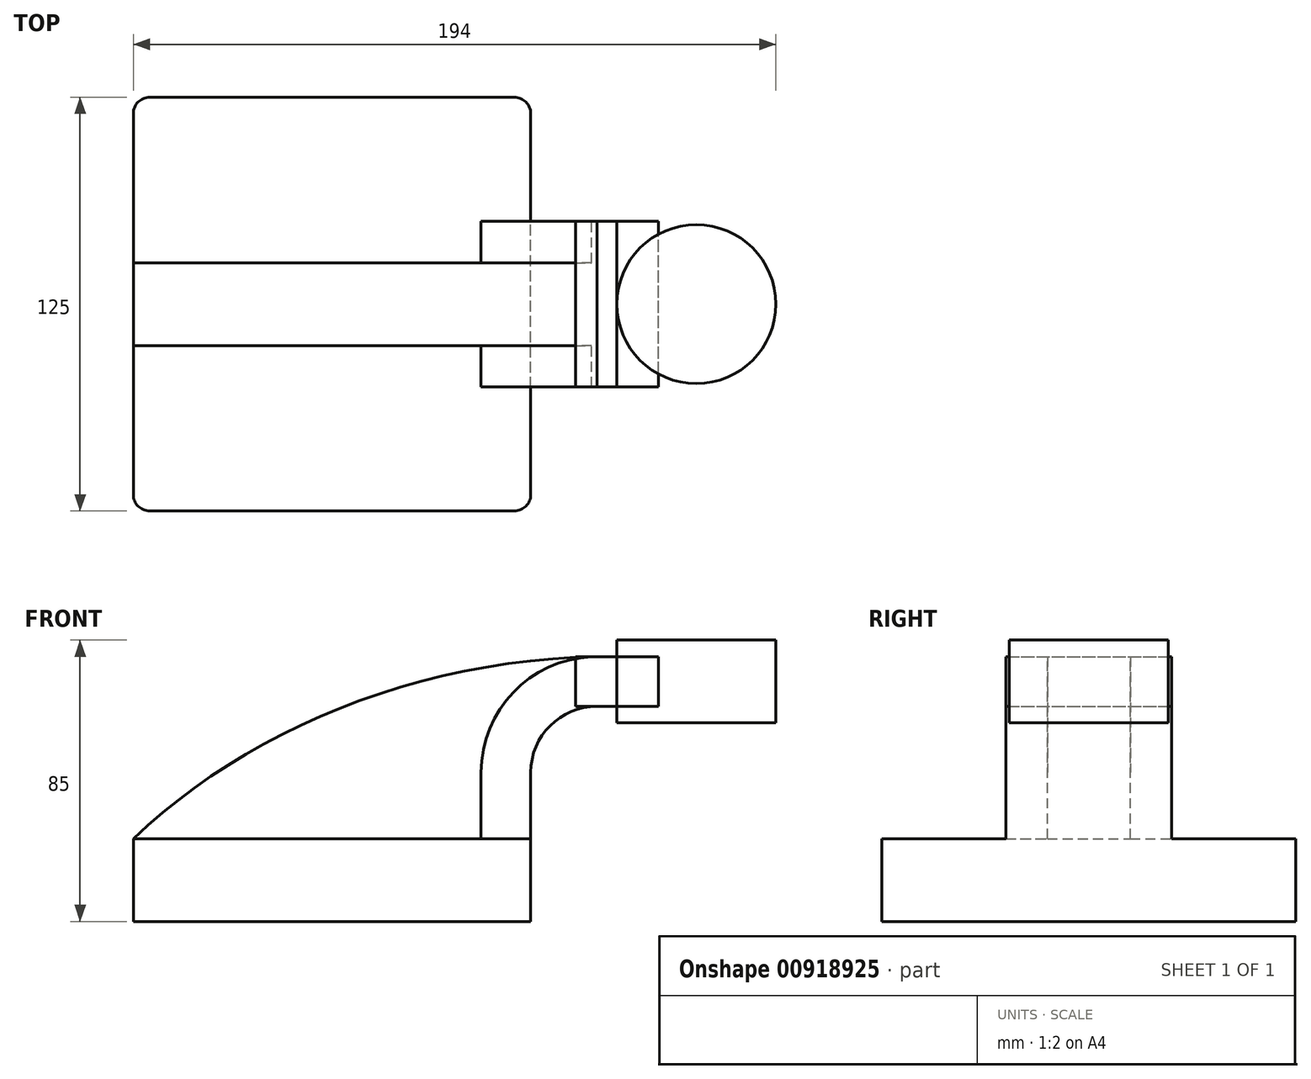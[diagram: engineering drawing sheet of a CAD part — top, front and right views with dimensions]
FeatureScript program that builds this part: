
annotation { "Feature Type Name" : "Feature", "Feature Type Description" : "" }
export const myFeature = defineFeature(function(context is Context, id is Id, definition is map)
    precondition{}
    {
        {
            var Q0;
            Q0=qCreatedBy(makeId("Front.planeOp"),FACE);
            var sketch = newSketch(context, id + "F0", { "sketchPlane" : qUnion([Q0])});
            skLineSegment(sketch, "E0.bottom", {"start": v(-60, 12.5) * mm, "end": v(60, 12.5) * mm});
            skLineSegment(sketch, "E0.top", {"start": v(-60, -12.5) * mm, "end": v(60, -12.5) * mm});
            skLineSegment(sketch, "E0.left", {"start": v(-60, 12.5) * mm, "end": v(-60, -12.5) * mm});
            skLineSegment(sketch, "E0.right", {"start": v(60, 12.5) * mm, "end": v(60, -12.5) * mm});
            skPoint(sketch, "E0.middle", {"position": v(0, 0) * mm});
            skLineSegment(sketch, "E1.bottom", {"start": v(134, 72.5) * mm, "end": v(86, 72.5) * mm});
            skLineSegment(sketch, "E1.top", {"start": v(134, 47.5) * mm, "end": v(86, 47.5) * mm});
            skLineSegment(sketch, "E1.left", {"start": v(134, 72.5) * mm, "end": v(134, 47.5) * mm});
            skLineSegment(sketch, "E1.right", {"start": v(86, 72.5) * mm, "end": v(86, 47.5) * mm});
            skPoint(sketch, "E1.middle", {"position": v(110, 60) * mm});
            skLineSegment(sketch, "E2", {"start": v(60, 12.5) * mm, "end": v(60, 32.5) * mm});
            skArc(sketch, "E3", {"start": v(60, 32.5) * mm, "mid": v(65.86, 46.64) * mm, "end": v(80, 52.5) * mm});
            skLineSegment(sketch, "E4", {"start": v(80, 52.5) * mm, "end": v(110, 52.5) * mm});
            skLineSegment(sketch, "E5.0", {"start": v(80, 67.5) * mm, "end": v(110, 67.5) * mm});
            skArc(sketch, "E5.1", {"start": v(45, 32.5) * mm, "mid": v(55.25, 57.25) * mm, "end": v(80, 67.5) * mm});
            skLineSegment(sketch, "E5.2", {"start": v(45, 12.5) * mm, "end": v(45, 32.5) * mm});
            skLineSegment(sketch, "E6", {"start": v(110, 47.5) * mm, "end": v(110, 72.5) * mm});
            skFitSpline(sketch, "E7", {"points": [v(-60, 12.5) * mm, v(80, 67.5) * mm], "startDerivative": vector(102.59, 97.87) * mm, "endDerivative": vector(165.07, 3.18) * mm});
            skSolve(sketch);
        }
        {
            var Q0;
            Q0=makeQuery(id+"F0.imprint","IMPRINT",FACE,{"disambiguationData":[TD([[makeQuery(id+"F0.imprint","IMPRINT",EDGE,{"derivedFrom":sQuery(id+"F0.wireOp",EDGE,"E0.top")}),1.0]])]});
            extrude(context, id + "F1", {"entities" : qUnion([Q0]), "depth" : 125 * mm, "offsetDistance" : 25 * mm, "symmetric" : true});
        }
        {
            var Q0;
            {var subQ1=sQuery(id+"F0.wireOp",EDGE,"E2");Q0=makeQuery(id+"F0.imprint","IMPRINT",FACE,{"disambiguationData":[TD([[makeQuery(id+"F0.imprint","IMPRINT",EDGE,{"derivedFrom":subQ1}),1.0]])]});}
            extrude(context, id + "F2", {"entities" : qUnion([Q0]), "operationType" : NewBodyOperationType.ADD, "depth" : 50 * mm, "offsetDistance" : 25 * mm, "symmetric" : true});
        }
        {
            var Q0;
            {var subQ3=sQuery(id+"F0.wireOp",EDGE,"E5.2");Q0=makeQuery(id+"F0.imprint","IMPRINT",FACE,{"disambiguationData":[TD([[makeQuery(id+"F0.imprint","IMPRINT",EDGE,{"derivedFrom":subQ3}),1.0]])]});}
            extrude(context, id + "F3", {"entities" : qUnion([Q0]), "operationType" : NewBodyOperationType.ADD, "depth" : 25 * mm, "offsetDistance" : 25 * mm, "symmetric" : true});
        }
        {
            var Q0;
            {var subQ0=sQuery(id+"F0.wireOp",EDGE,"E1.left");Q0=makeQuery(id+"F0.imprint","IMPRINT",FACE,{"disambiguationData":[TD([[makeQuery(id+"F0.imprint","IMPRINT",EDGE,{"derivedFrom":subQ0}),-1.0]])]});}
            var Q1;
            Q1=sQuery(id+"F0.wireOp",EDGE,"E6");
            revolve(context, id + "F4", {"operationType" : NewBodyOperationType.ADD, "surfaceOperationType" : NewSurfaceOperationType.NEW, "entities" : qUnion([Q0]), "axis" : qUnion([Q1]), "revolveType" : RevolveType.FULL});
        }
        {
            var Q0;
            Q0=makeQuery(id+"F1.opExtrude","CAP_EDGE",EDGE,{"disambiguationData":[OSD([sQuery(id+"F0.wireOp",EDGE,"E0.left")])],"isStart":false});
            var Q1;
            Q1=makeQuery(id+"F1.opExtrude","CAP_EDGE",EDGE,{"disambiguationData":[OSD([sQuery(id+"F0.wireOp",EDGE,"E0.right")])],"isStart":false});
            var Q2;
            Q2=makeQuery(id+"F1.opExtrude","CAP_EDGE",EDGE,{"disambiguationData":[OSD([sQuery(id+"F0.wireOp",EDGE,"E0.right")])],"isStart":true});
            var Q3;
            Q3=makeQuery(id+"F1.opExtrude","CAP_EDGE",EDGE,{"disambiguationData":[OSD([sQuery(id+"F0.wireOp",EDGE,"E0.left")])],"isStart":true});
            fillet(context, id + "F5", {"entities" : qUnion([Q0, Q1, Q2, Q3]), "radius" : 5 * mm, "tangentPropagation" : true, "allowEdgeOverflow" : false});
        }
        {
            var Q0;
            Q0=makeQuery(id+"F2.opExtrude","SWEPT_FACE",FACE,{"disambiguationData":[OSD([sQuery(id+"F0.wireOp",EDGE,"E1.right")])]});
            extrude(context, id + "F6", {"entities" : qUnion([Q0]), "depth" : 25 * mm, "offsetDistance" : 25 * mm, "symmetric" : true});
        }
    });
